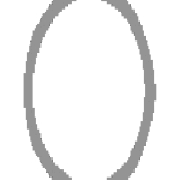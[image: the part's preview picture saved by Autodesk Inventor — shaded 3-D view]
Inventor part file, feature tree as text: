
AUTODESK INVENTOR PART (.ipt)
format: ipt  version: 2021 (Build 250183000, 183)  size: 136,192 bytes
history: native  units: in
note: dims shown in document units (in); Inventor stores cm internally (conversion verified against a paired STEP export)
features: other x4, plane x4, sketch x4, extrude x1, boolean_combine x1
ambient origin geometry x8: Origin, YZ Plane, XZ Plane, XY Plane, X Axis, Y Axis, Z Axis, Center Point
bodies: Solid1 (feature_tree), Body (feature_tree), Solid2 (feature_tree)
feature tree (14):
  other  "Driven Length"
  other  "Frame Generator"
  other  "Start Plane"
  other  "End Plane"
  plane  "Work Plane4"
  plane  "Work Plane5"
  plane  "Work Plane6"
  extrude  "Extrusion3"  Depth=0.065in
  boolean_combine  "Combine1"
  sketch  "Sketch"  dims[d5=1.3416in d6=0.12in d7=0.0in d8=90.0deg d9=1.3416in d10=0.12in d11=0.0in]
  sketch  "Sketch2"  dims[d0=1.0in d1=0.065in]
  plane  "Work Plane3"
  sketch  "Sketch3"  dims[d2=1.3416in]
  sketch  "Sketch4"  dims[d4=-0.0in]
